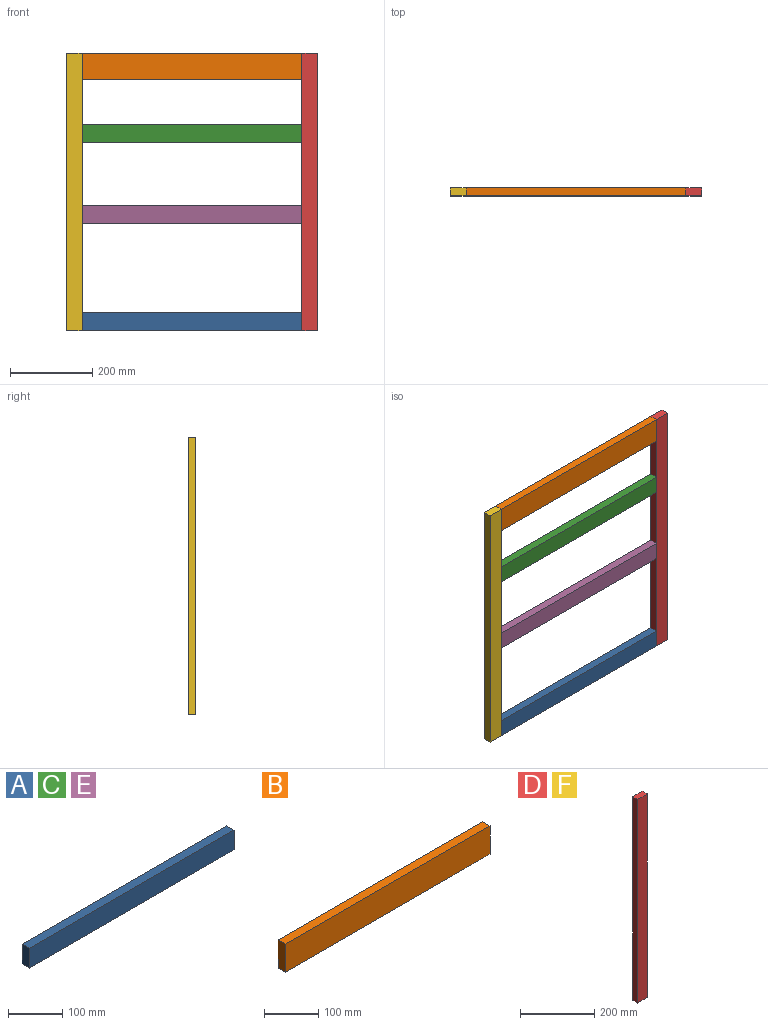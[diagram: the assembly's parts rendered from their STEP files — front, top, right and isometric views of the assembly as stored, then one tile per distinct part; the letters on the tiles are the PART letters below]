
ASSEMBLY  parts=6 mates=5
PART A: 6 faces, bbox 533.4x19.1x44.5 mm
  f0: plane 533.4x19.05mm, normal (0,0,1), area 10161.3mm2, adj f1,f3,f4,f5
  f1: plane 44.45x19.05mm, normal (-1,0,0), area 846.8mm2, adj f0,f2,f4,f5
  f2: plane 533.4x19.05mm, normal (0,0,-1), area 10161.3mm2, adj f1,f3,f4,f5
  f3: plane 44.45x19.05mm, normal (1,0,0), area 846.8mm2, adj f0,f2,f4,f5
  f4: plane 533.4x44.45mm, normal (0,-1,0), area 23709.6mm2, adj f0,f1,f2,f3
  f5: plane 533.4x44.45mm, normal (0,1,0), area 23709.6mm2, adj f0,f1,f2,f3
PART B: 6 faces, bbox 533.4x19.1x63.5 mm
  f0: plane 533.4x19.05mm, normal (0,0,1), area 10161.3mm2, adj f1,f3,f4,f5
  f1: plane 63.5x19.05mm, normal (-1,0,0), area 1209.7mm2, adj f0,f2,f4,f5
  f2: plane 533.4x19.05mm, normal (0,0,-1), area 10161.3mm2, adj f1,f3,f4,f5
  f3: plane 63.5x19.05mm, normal (1,0,0), area 1209.7mm2, adj f0,f2,f4,f5
  f4: plane 533.4x63.5mm, normal (0,-1,0), area 33870.9mm2, adj f0,f1,f2,f3
  f5: plane 533.4x63.5mm, normal (0,1,0), area 33870.9mm2, adj f0,f1,f2,f3
PART C: same geometry as A
PART D: 6 faces, bbox 38.1x19.1x673.1 mm
  f0: plane 38.1x19.05mm, normal (0,0,1), area 725.8mm2, adj f1,f3,f4,f5
  f1: plane 673.1x19.05mm, normal (-1,0,0), area 12822.6mm2, adj f0,f2,f4,f5
  f2: plane 38.1x19.05mm, normal (0,0,-1), area 725.8mm2, adj f1,f3,f4,f5
  f3: plane 673.1x19.05mm, normal (1,0,0), area 12822.6mm2, adj f0,f2,f4,f5
  f4: plane 673.1x38.1mm, normal (0,-1,0), area 25645.1mm2, adj f0,f1,f2,f3
  f5: plane 673.1x38.1mm, normal (0,1,0), area 25645.1mm2, adj f0,f1,f2,f3
PART E: same geometry as A
PART F: same geometry as D
PLACE A t=(102.37,95.73,-747.44)mm
PLACE B t=(102.37,95.73,-137.84)mm
PLACE C t=(102.37,95.73,-290.24)mm
PLACE D t=(140.47,95.73,-747.44)mm
PLACE E t=(102.37,95.73,-487.09)mm
PLACE F t=(-431.03,95.73,-747.44)mm
MATE fastened E.f4 <-> C.f4  axis (0,-1,0) through (102.37,76.68,-442.64)mm
MATE fastened B.f4 <-> C.f4  axis (0,-1,0) through (102.37,76.68,-137.84)mm
MATE fastened A.f4 <-> D.f4  axis (0,-1,0) through (102.37,76.68,-747.44)mm
MATE fastened B.f4 <-> D.f4  axis (0,-1,0) through (102.37,76.68,-74.34)mm
MATE fastened F.f4 <-> B.f4  axis (0,-1,0) through (-431.03,76.68,-74.34)mm
